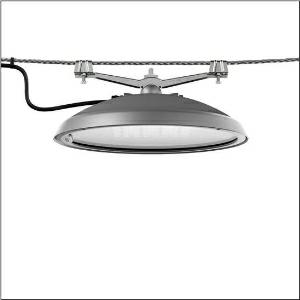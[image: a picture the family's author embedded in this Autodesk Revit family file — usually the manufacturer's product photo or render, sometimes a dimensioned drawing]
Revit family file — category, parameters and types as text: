
# Revit family: dl_50_iq_mini___st1_0s_5xa248w41f08re_c8d8
name_source: partatom
category: Lighting Fixtures
units: mm (PartAtom-declared; Revit-internal decimal feet)

## family parameters
Cut with Voids When Loaded = No
Host = Face
Light Source = No
Part Type = Normal
Room Calculation Point = No
Round Connector Dimension = Use Diameter
Shared = No

## types (1)
- --- (1 x LED, 5990 lm, 33.8 W, 4000K)
    Apparent Load = 34 VA
    CIE Flux Codes = 37 72 97 100 100
    Color Rendering = 70
    Color Temperature = 4000K
    Default Elevation = 1800 mm
    Description = DL 50 iQ mini, catenary luminaire, primary light control with lens, of PMMA, primary optical cover: cover, of toughened safety glass, transparent, light distribution: ST1.0s, light emission: direct distribution, primary light characteristic: symmetric, installation type: suspended mounting, LED, High Power LED, rated luminous flux: 5.990lm, luminous efficacy: 177lm/W, light colour: 740, colour temperature: 4000K, control gear: iQ Street-Remote, control: optimised constant luminous flux control (CLO 2.0), Desk-Remote (wireless, voltage-free reading and setting of iQ features in the workshop via application-optimized NFC function/RFID function), Light-Fading, Smart-Wire, Night-Set, Lumen-Switch, Temp-Guard, Auto-Match, Street-Remote, mains connection: 230..240V, AC, 50/60Hz, start of lifetime: 34W, end of service life: 35W, reduction: 16W, luminaire housing, of diecast aluminium, powder-coated, SITECO metallic grey (DB 702S), diameter: 500mm, height: 115mm, mounting height: 4..12m, protection rating (complete): IP66, insulation class (complete): insulation class II (safety insulation), certification: CE, ENEC, ENEC+, VDE, impact resistance: IK08, permissible operating ambient temperature for outdoor applications: -25..+40°C, standard-compliant lighting for roads and squares, packaging unit: 1 piece

Light Distribution: ST1.0s
    Height = 124 mm  [stored 0.406824 ft]
    Lamp = 1 x LED
    Lamp Light Flux = 5990 lm
    Lamp Power = 33.8 W
    Lamp count = 1
    Length = 500 mm
    Luminous efficacy = 177 lm/W
    Manufacturer = Siteco
    ModVariant = No
    Model = 5XA248W41F08RE
    Number of Poles = 1
    OnlyDefault = Yes
    Power Factor = 1
    Product Name = DL 50 iQ mini | ST1.0s
    Product group = catenary luminaire
    ProductGroupID = 6300
    Protection Class = Protection class II
    Protection Degree = IP 66
    RLX_Detail_Level = 1
    RLX_Emergency_Light_Flux = 0 lm
    RLX_Emergency_Type = 0
    RLX_Emergency_Type_DB = No
    RlxData = <blob elided: 123541 chars, md5=cc7f639e>
    Socket = socket
    Standby Power = 0 W
    System Light Flux = 5990 lm
    System Power = 34 W
    Type Comments = factory setting: luminous flux: 100 % | dim-lin: 254 | 359 mA
    Type Image = l_1242791.jpg
    URL = http://relux.com
    VarID = @adj_140211
    Voltage = 0 V
    Weight = 0.00 kg
    Width = 0 mm  [stored 0 ft]

note: [stored X ft] marks values corroborated as IEEE doubles in the binary element streams (Revit-internal decimal feet)

## geometry (parser evidence)
native form markers: Blend x4, Sweep x12
no freeform markers — native parametric forms only
